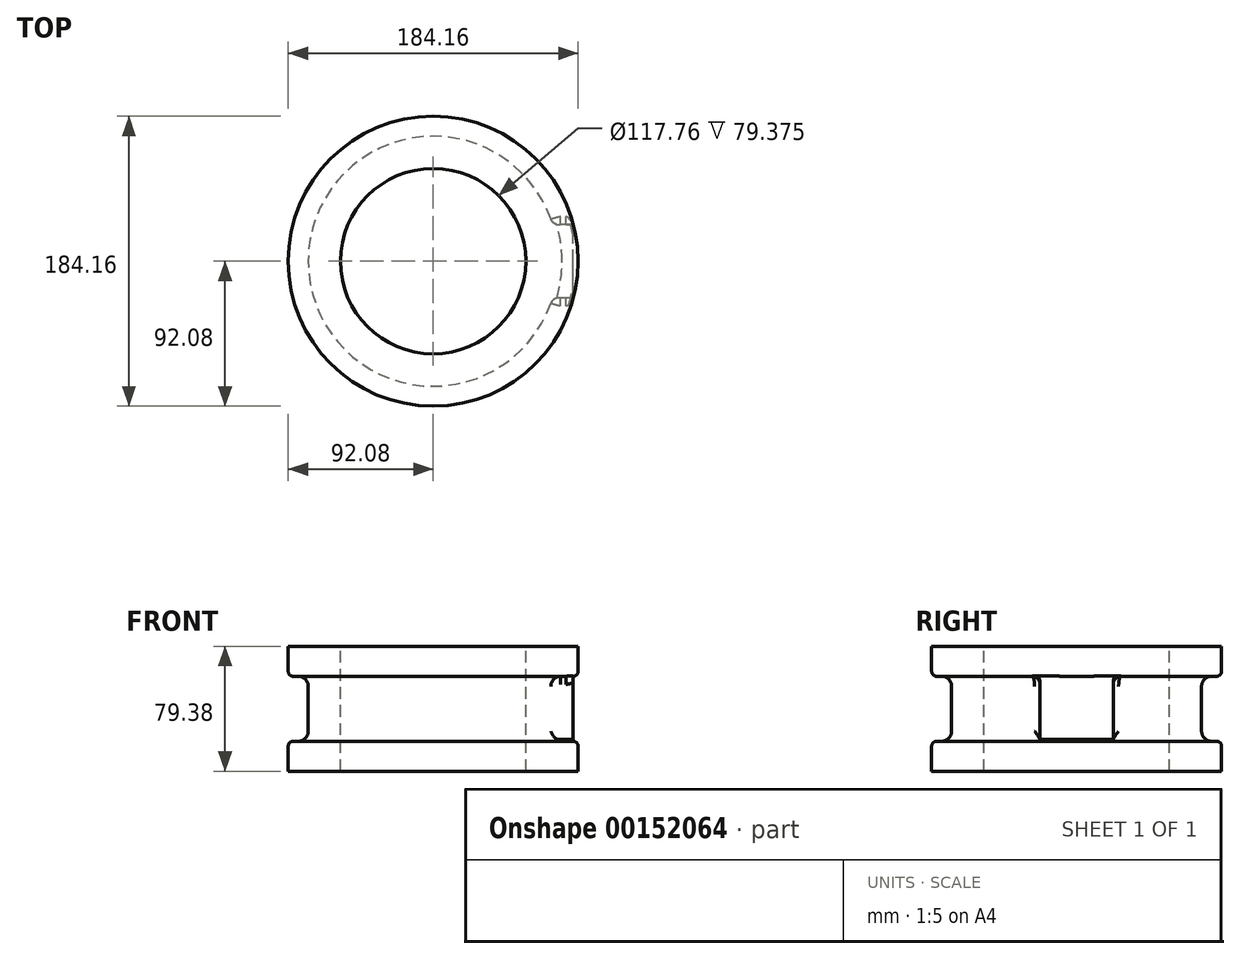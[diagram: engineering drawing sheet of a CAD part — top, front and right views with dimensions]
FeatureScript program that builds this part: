
annotation { "Feature Type Name" : "Feature", "Feature Type Description" : "" }
export const myFeature = defineFeature(function(context is Context, id is Id, definition is map)
    precondition{}
    {
        {
            var Q0;
            Q0=qCreatedBy(makeId("Front.planeOp"),FACE);
            var sketch = newSketch(context, id + "F0", { "sketchPlane" : qUnion([Q0])});
            skLineSegment(sketch, "E0", {"start": v(0, 110.9) * mm, "end": v(0, -142.4) * mm, "construction": true});
            skLineSegment(sketch, "E1", {"start": v(92.08, 0) * mm, "end": v(92.08, 15.88) * mm});
            skLineSegment(sketch, "E2", {"start": v(88.9, 19.05) * mm, "end": v(85.73, 19.05) * mm});
            skLineSegment(sketch, "E3", {"start": v(79.38, 25.4) * mm, "end": v(79.38, 53.98) * mm});
            skLineSegment(sketch, "E4", {"start": v(85.73, 60.33) * mm, "end": v(88.9, 60.33) * mm});
            skLineSegment(sketch, "E5", {"start": v(92.08, 63.5) * mm, "end": v(92.08, 79.38) * mm});
            skLineSegment(sketch, "E6", {"start": v(92.08, 79.38) * mm, "end": v(58.88, 79.38) * mm});
            skLineSegment(sketch, "E7", {"start": v(58.88, 79.38) * mm, "end": v(58.88, 0) * mm});
            skLineSegment(sketch, "E8.trimOffspring", {"start": v(58.88, 0) * mm, "end": v(92.08, 0) * mm});
            skPoint(sketch, "E9.end.orphan", {"position": v(18.5, 79.38) * mm});
            skPoint(sketch, "E10.end.orphan", {"position": v(21.68, 0) * mm});
            skPoint(sketch, "E11.visualSharp", {"position": v(79.38, 60.33) * mm});
            skArc(sketch, "E11.filletArc", {"start": v(85.73, 60.33) * mm, "mid": v(81.23, 58.47) * mm, "end": v(79.38, 53.98) * mm});
            skPoint(sketch, "E12.visualSharp", {"position": v(79.38, 19.05) * mm});
            skArc(sketch, "E12.filletArc", {"start": v(79.38, 25.4) * mm, "mid": v(81.23, 20.9) * mm, "end": v(85.73, 19.05) * mm});
            skPoint(sketch, "E13.visualSharp", {"position": v(92.08, 19.05) * mm});
            skArc(sketch, "E13.filletArc", {"start": v(92.08, 15.88) * mm, "mid": v(91.15, 18.12) * mm, "end": v(88.9, 19.05) * mm});
            skPoint(sketch, "E14.visualSharp", {"position": v(92.08, 60.33) * mm});
            skArc(sketch, "E14.filletArc", {"start": v(88.9, 60.33) * mm, "mid": v(91.15, 61.25) * mm, "end": v(92.08, 63.5) * mm});
            skSolve(sketch);
        }
        {
            var Q0;
            Q0 = qSketchRegion(id + "F0", true);
            var Q1;
            Q1=sQuery(id+"F0.wireOp",EDGE,"E0");
            revolve(context, id + "F1", {"entities" : qUnion([Q0]), "axis" : qUnion([Q1]), "revolveType" : RevolveType.FULL});
        }
        {
            var Q0;
            Q0=qCreatedBy(makeId("Right.planeOp"),FACE);
            cPlane(context, id + "F2", {"entities" : qUnion([Q0]), "cplaneType" : CPlaneType.OFFSET, "offset" : 63.5 * mm, "width" : 152.4 * mm, "height" : 152.4 * mm});
        }
        {
            var Q0;
            Q0=qCreatedBy(id+"F2.planeOp",FACE);
            var sketch = newSketch(context, id + "F3", { "sketchPlane" : qUnion([Q0])});
            skLineSegment(sketch, "E15.bottom", {"start": v(-23.3, 60.68) * mm, "end": v(23.3, 60.68) * mm});
            skLineSegment(sketch, "E15.top", {"start": v(-23.3, 20.34) * mm, "end": v(23.3, 20.34) * mm});
            skLineSegment(sketch, "E15.left", {"start": v(-23.3, 60.68) * mm, "end": v(-23.3, 20.34) * mm});
            skLineSegment(sketch, "E15.right", {"start": v(23.3, 60.68) * mm, "end": v(23.3, 20.34) * mm});
            skPoint(sketch, "E15.middle", {"position": v(0, 40.5) * mm});
            skSolve(sketch);
        }
        {
            var Q0;
            Q0 = qSketchRegion(id + "F3", true);
            extrude(context, id + "F4", {"entities" : qUnion([Q0]), "operationType" : NewBodyOperationType.ADD, "depth" : 25.4 * mm});
        }
        {
            var Q0;
            Q0=makeQuery(id+"F4.boolean.opBoolean","INTERSECT",EDGE,{"derivedFrom":[makeQuery(id+"F1.opRevolve","SWEPT_FACE",FACE,{"disambiguationData":[OSD([sQuery(id+"F0.wireOp",EDGE,"E3")])]}),makeQuery(id+"F4.opExtrude","SWEPT_FACE",FACE,{"disambiguationData":[OSD([sQuery(id+"F3.wireOp",EDGE,"E15.left")])]})]});
            var Q1;
            Q1=makeQuery(id+"F4.boolean.opBoolean","INTERSECT",EDGE,{"derivedFrom":[makeQuery(id+"F1.opRevolve","SWEPT_FACE",FACE,{"disambiguationData":[OSD([sQuery(id+"F0.wireOp",EDGE,"E3")])]}),makeQuery(id+"F4.opExtrude","SWEPT_FACE",FACE,{"disambiguationData":[OSD([sQuery(id+"F3.wireOp",EDGE,"E15.right")])]})]});
            fillet(context, id + "F5", {"entities" : qUnion([Q0, Q1]), "radius" : 5.08 * mm, "tangentPropagation" : true, "allowEdgeOverflow" : false});
        }
    });
